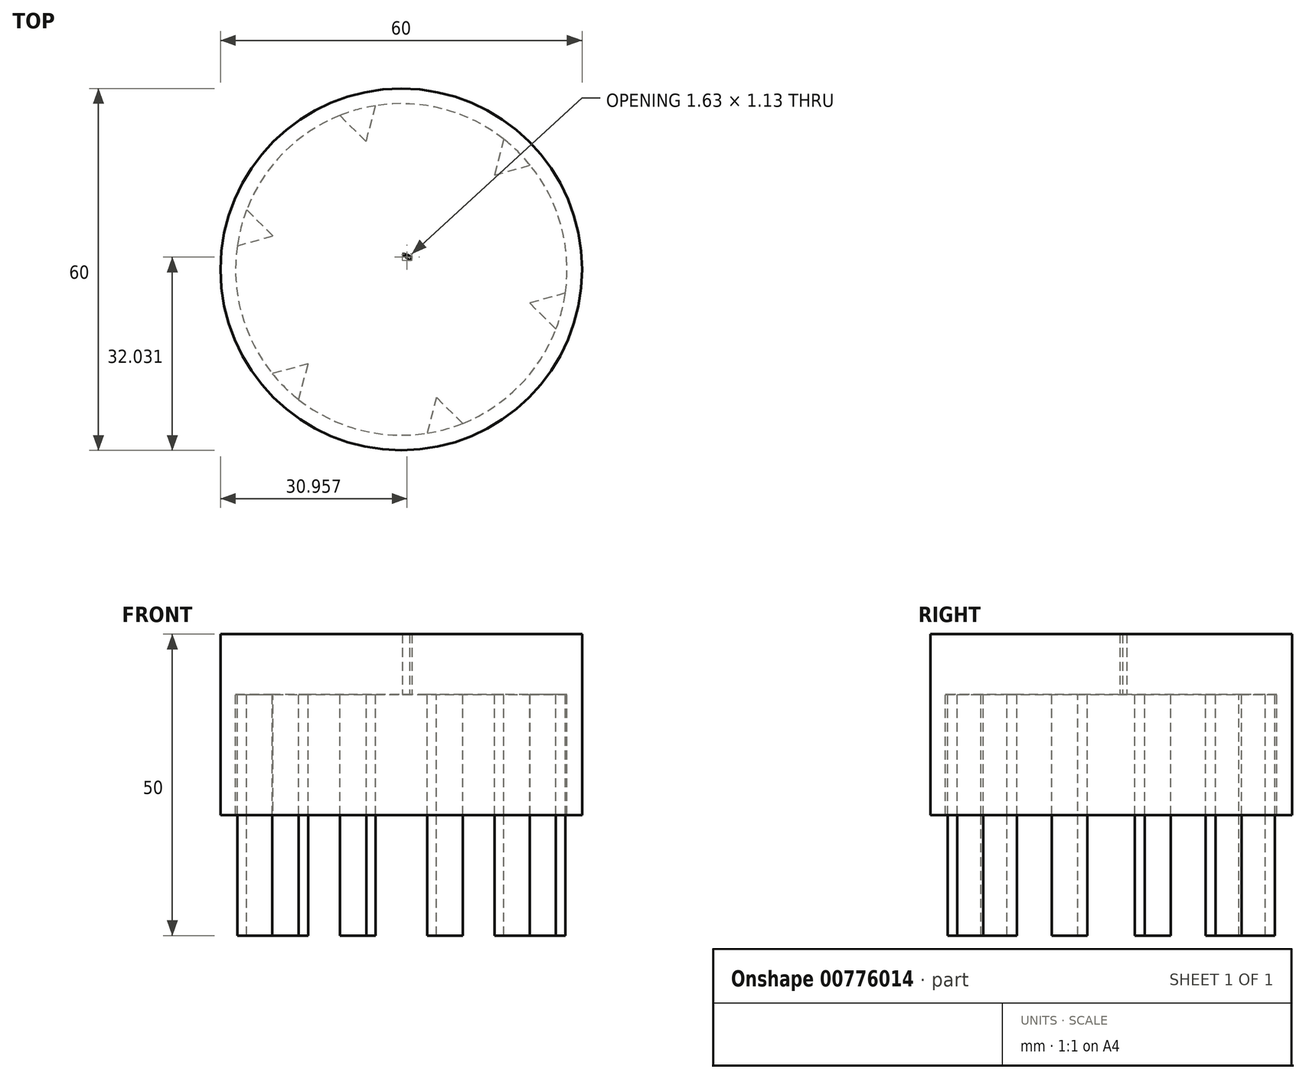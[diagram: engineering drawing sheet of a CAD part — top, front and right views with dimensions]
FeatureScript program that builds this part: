
annotation { "Feature Type Name" : "Feature", "Feature Type Description" : "" }
export const myFeature = defineFeature(function(context is Context, id is Id, definition is map)
    precondition{}
    {
        {
            var Q0;
            Q0=qCreatedBy(makeId("Top.planeOp"),FACE);
            var sketch = newSketch(context, id + "F0", { "sketchPlane" : qUnion([Q0])});
            skCircle(sketch, "E0", {"center": v(0, 0) * mm, "radius": 2.6 * mm});
            skLineSegment(sketch, "E1", {"start": v(0, 0) * mm, "end": v(1.77, 1.9) * mm});
            skLineSegment(sketch, "E2", {"start": v(-0.47, 3.17) * mm, "end": v(3.2, -0.24) * mm});
            skSolve(sketch);
        }
        {
            var Q0;
            {var subQ0=sQuery(id+"F0.wireOp",EDGE,"E2");var subQ1=sQuery(id+"F0.wireOp",EDGE,"E0");var subQ2=makeQuery(id+"F0.imprint","INTERSECT",VERTEX,{"disambiguationData":[OD(0.0)],"derivedFrom":[subQ1,subQ0]});Q0=makeQuery(id+"F0.imprint","IMPRINT",FACE,{"disambiguationData":[TD([[makeQuery(id+"F0.imprint","IMPRINT",EDGE,{"disambiguationData":[TD([[subQ2,1.0]])],"derivedFrom":subQ1}),1.0]])]});}
            var sketch = newSketch(context, id + "F1", { "sketchPlane" : qUnion([Q0])});
            skCircle(sketch, "E3", {"center": v(0, 0) * mm, "radius": 30 * mm});
            skSolve(sketch);
        }
        {
            var Q0;
            Q0=makeQuery(id+"F1.imprint","IMPRINT",FACE,{"disambiguationData":[TD([[makeQuery(id+"F1.imprint","IMPRINT",EDGE,{"derivedFrom":sQuery(id+"F1.wireOp",EDGE,"E3")}),1.0]])]});
            extrude(context, id + "F2", {"entities" : qUnion([Q0]), "depth" : 10 * mm, "offsetDistance" : 25.4 * mm});
        }
        {
            var Q0;
            Q0=makeQuery(id+"F2.opExtrude","CAP_FACE",FACE,{"disambiguationData":[OSD([sQuery(id+"F0.wireOp",EDGE,"E0"),sQuery(id+"F0.wireOp",EDGE,"E2"),sQuery(id+"F1.wireOp",EDGE,"E3")])],"isStart":true});
            var sketch = newSketch(context, id + "F3", { "sketchPlane" : qUnion([Q0])});
            skCircle(sketch, "E4", {"center": v(0, 0) * mm, "radius": 27.5 * mm});
            skSolve(sketch);
        }
        {
            var Q0;
            Q0=makeQuery(id+"F3.imprint","IMPRINT",FACE,{"disambiguationData":[TD([[makeQuery(id+"F3.imprint","IMPRINT",EDGE,{"derivedFrom":sQuery(id+"F3.wireOp",EDGE,"E4")}),1.0]])]});
            var sketch = newSketch(context, id + "F4", { "sketchPlane" : qUnion([Q0])});
            skCircle(sketch, "E5.cCircle", {"center": v(0, 0) * mm, "radius": 30 * mm, "construction": true});
            skCircle(sketch, "E6", {"center": v(0, 0) * mm, "radius": 22 * mm});
            skCircle(sketch, "E7.cCircle", {"center": v(21.08, -21.35) * mm, "radius": 8 * mm, "construction": true});
            skLineSegment(sketch, "E7.0", {"start": v(15.46, -15.65) * mm, "end": v(28.82, -19.32) * mm});
            skLineSegment(sketch, "E7.1", {"start": v(28.82, -19.32) * mm, "end": v(18.96, -29.06) * mm});
            skLineSegment(sketch, "E7.2", {"start": v(18.96, -29.06) * mm, "end": v(15.46, -15.65) * mm});
            skCircle(sketch, "E8.cCircle", {"center": v(-7.95, -28.93) * mm, "radius": 8 * mm, "construction": true});
            skLineSegment(sketch, "E8.0", {"start": v(-5.83, -21.21) * mm, "end": v(-2.33, -34.62) * mm});
            skLineSegment(sketch, "E8.1", {"start": v(-2.33, -34.62) * mm, "end": v(-15.69, -30.95) * mm});
            skLineSegment(sketch, "E8.2", {"start": v(-15.69, -30.95) * mm, "end": v(-5.83, -21.21) * mm});
            skCircle(sketch, "E9.cCircle", {"center": v(-29.03, -7.58) * mm, "radius": 8 * mm, "construction": true});
            skLineSegment(sketch, "E9.0", {"start": v(-21.29, -5.56) * mm, "end": v(-31.15, -15.3) * mm});
            skLineSegment(sketch, "E9.1", {"start": v(-31.15, -15.3) * mm, "end": v(-34.65, -1.9) * mm});
            skLineSegment(sketch, "E9.2", {"start": v(-34.65, -1.9) * mm, "end": v(-21.29, -5.56) * mm});
            skCircle(sketch, "E10.cCircle", {"center": v(7.95, 28.93) * mm, "radius": 8 * mm, "construction": true});
            skLineSegment(sketch, "E10.0", {"start": v(5.83, 21.21) * mm, "end": v(2.33, 34.62) * mm});
            skLineSegment(sketch, "E10.1", {"start": v(2.33, 34.62) * mm, "end": v(15.69, 30.95) * mm});
            skLineSegment(sketch, "E10.2", {"start": v(15.69, 30.95) * mm, "end": v(5.83, 21.21) * mm});
            skCircle(sketch, "E11.cCircle", {"center": v(29.03, 7.58) * mm, "radius": 8 * mm, "construction": true});
            skLineSegment(sketch, "E11.0", {"start": v(21.29, 5.56) * mm, "end": v(31.15, 15.3) * mm});
            skLineSegment(sketch, "E11.1", {"start": v(31.15, 15.3) * mm, "end": v(34.65, 1.9) * mm});
            skLineSegment(sketch, "E11.2", {"start": v(34.65, 1.9) * mm, "end": v(21.29, 5.56) * mm});
            skCircle(sketch, "E12.cCircle", {"center": v(-21.08, 21.35) * mm, "radius": 8 * mm, "construction": true});
            skLineSegment(sketch, "E12.0", {"start": v(-15.46, 15.65) * mm, "end": v(-28.82, 19.32) * mm});
            skLineSegment(sketch, "E12.1", {"start": v(-28.82, 19.32) * mm, "end": v(-18.96, 29.06) * mm});
            skLineSegment(sketch, "E12.2", {"start": v(-18.96, 29.06) * mm, "end": v(-15.46, 15.65) * mm});
            skSolve(sketch);
        }
        {
            var Q0;
            {var subQ1=sQuery(id+"F4.wireOp",EDGE,"E8.0");var subQ3=makeQuery(id+"F3.imprint","IMPRINT",EDGE,{"derivedFrom":sQuery(id+"F3.wireOp",EDGE,"E4")});var subQ4=makeQuery(id+"F4.imprint","INTERSECT",VERTEX,{"derivedFrom":[subQ3,subQ1]});Q0=makeQuery(id+"F4.imprint","IMPRINT",FACE,{"disambiguationData":[TD([[makeQuery(id+"F4.imprint","IMPRINT",EDGE,{"disambiguationData":[TD([[subQ4,1.0]])],"derivedFrom":subQ3}),1.0]])]});}
            var Q1;
            {var subQ1=sQuery(id+"F4.wireOp",EDGE,"E7.0");var subQ3=makeQuery(id+"F3.imprint","IMPRINT",EDGE,{"derivedFrom":sQuery(id+"F3.wireOp",EDGE,"E4")});var subQ4=makeQuery(id+"F4.imprint","INTERSECT",VERTEX,{"derivedFrom":[subQ3,subQ1]});Q1=makeQuery(id+"F4.imprint","IMPRINT",FACE,{"disambiguationData":[TD([[makeQuery(id+"F4.imprint","IMPRINT",EDGE,{"disambiguationData":[TD([[subQ4,1.0]])],"derivedFrom":subQ3}),1.0]])]});}
            var Q2;
            {var subQ1=sQuery(id+"F4.wireOp",EDGE,"E10.0");var subQ3=makeQuery(id+"F3.imprint","IMPRINT",EDGE,{"derivedFrom":sQuery(id+"F3.wireOp",EDGE,"E4")});var subQ4=makeQuery(id+"F4.imprint","INTERSECT",VERTEX,{"derivedFrom":[subQ3,subQ1]});Q2=makeQuery(id+"F4.imprint","IMPRINT",FACE,{"disambiguationData":[TD([[makeQuery(id+"F4.imprint","IMPRINT",EDGE,{"disambiguationData":[TD([[subQ4,1.0]])],"derivedFrom":subQ3}),1.0]])]});}
            var Q3;
            {var subQ1=sQuery(id+"F4.wireOp",EDGE,"E11.0");var subQ3=makeQuery(id+"F3.imprint","IMPRINT",EDGE,{"derivedFrom":sQuery(id+"F3.wireOp",EDGE,"E4")});var subQ4=makeQuery(id+"F4.imprint","INTERSECT",VERTEX,{"derivedFrom":[subQ3,subQ1]});Q3=makeQuery(id+"F4.imprint","IMPRINT",FACE,{"disambiguationData":[TD([[makeQuery(id+"F4.imprint","IMPRINT",EDGE,{"disambiguationData":[TD([[subQ4,1.0]])],"derivedFrom":subQ3}),1.0]])]});}
            var Q4;
            {var subQ1=sQuery(id+"F4.wireOp",EDGE,"E12.0");var subQ3=makeQuery(id+"F3.imprint","IMPRINT",EDGE,{"derivedFrom":sQuery(id+"F3.wireOp",EDGE,"E4")});var subQ4=makeQuery(id+"F4.imprint","INTERSECT",VERTEX,{"derivedFrom":[subQ3,subQ1]});Q4=makeQuery(id+"F4.imprint","IMPRINT",FACE,{"disambiguationData":[TD([[makeQuery(id+"F4.imprint","IMPRINT",EDGE,{"disambiguationData":[TD([[subQ4,1.0]])],"derivedFrom":subQ3}),1.0]])]});}
            var Q5;
            {var subQ1=sQuery(id+"F4.wireOp",EDGE,"E9.0");var subQ3=makeQuery(id+"F3.imprint","IMPRINT",EDGE,{"derivedFrom":sQuery(id+"F3.wireOp",EDGE,"E4")});var subQ4=makeQuery(id+"F4.imprint","INTERSECT",VERTEX,{"derivedFrom":[subQ3,subQ1]});Q5=makeQuery(id+"F4.imprint","IMPRINT",FACE,{"disambiguationData":[TD([[makeQuery(id+"F4.imprint","IMPRINT",EDGE,{"disambiguationData":[TD([[subQ4,1.0]])],"derivedFrom":subQ3}),1.0]])]});}
            extrude(context, id + "F5", {"entities" : qUnion([Q0, Q1, Q2, Q3, Q4, Q5]), "operationType" : NewBodyOperationType.ADD, "depth" : 40 * mm, "offsetDistance" : 25 * mm});
        }
        {
            var Q0;
            Q0=makeQuery(id+"F3.imprint","IMPRINT",FACE,{"disambiguationData":[TD([[makeQuery(id+"F3.imprint","IMPRINT",EDGE,{"derivedFrom":sQuery(id+"F3.wireOp",EDGE,"E4")}),-1.0]])]});
            extrude(context, id + "F6", {"entities" : qUnion([Q0]), "operationType" : NewBodyOperationType.ADD, "depth" : 20 * mm, "offsetDistance" : 25 * mm});
        }
    });
